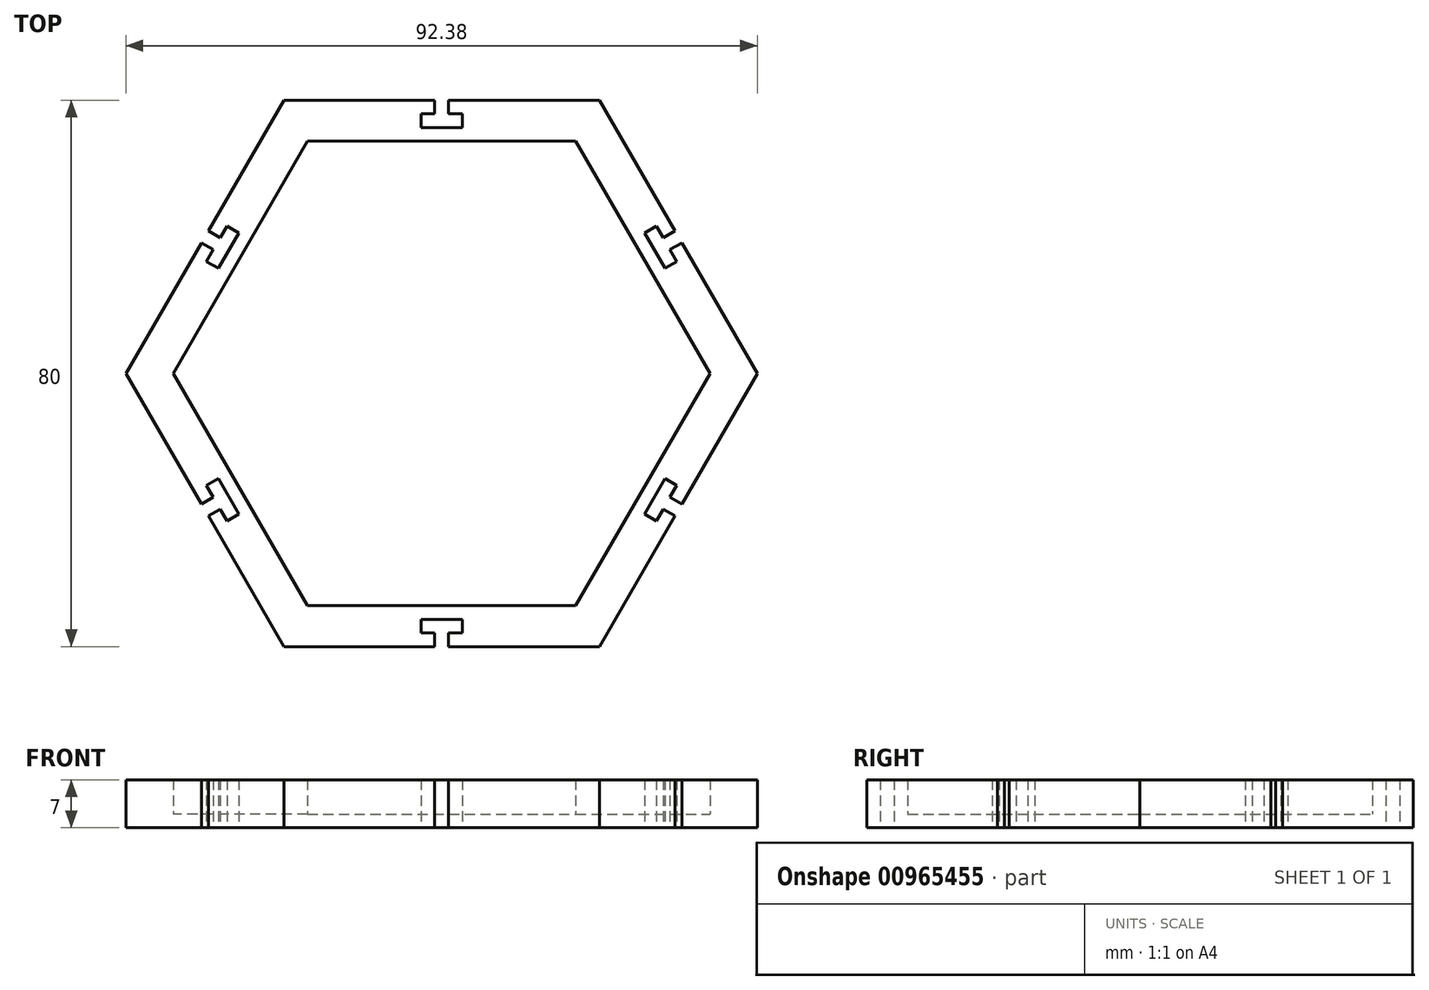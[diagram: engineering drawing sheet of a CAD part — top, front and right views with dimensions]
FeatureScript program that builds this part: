
annotation { "Feature Type Name" : "Feature", "Feature Type Description" : "" }
export const myFeature = defineFeature(function(context is Context, id is Id, definition is map)
    precondition{}
    {
        {
            var Q0;
            Q0=qCreatedBy(makeId("Top.planeOp"),FACE);
            var sketch = newSketch(context, id + "F0", { "sketchPlane" : qUnion([Q0])});
            skLineSegment(sketch, "E0", {"start": v(-13.7, -43.48) * mm, "end": v(8.4, -43.48) * mm});
            skLineSegment(sketch, "E1", {"start": v(9.4, -3.48) * mm, "end": v(9.4, -43.48) * mm, "construction": true});
            skLineSegment(sketch, "E2", {"start": v(8.4, -43.48) * mm, "end": v(8.4, -41.48) * mm});
            skLineSegment(sketch, "E3", {"start": v(8.4, -41.48) * mm, "end": v(6.4, -41.48) * mm});
            skLineSegment(sketch, "E4", {"start": v(6.4, -41.48) * mm, "end": v(6.4, -39.48) * mm});
            skLineSegment(sketch, "E5", {"start": v(6.4, -39.48) * mm, "end": v(12.4, -39.48) * mm});
            skLineSegment(sketch, "E6", {"start": v(12.4, -39.48) * mm, "end": v(12.4, -41.48) * mm});
            skLineSegment(sketch, "E7", {"start": v(12.4, -41.48) * mm, "end": v(10.4, -41.48) * mm});
            skLineSegment(sketch, "E8", {"start": v(10.4, -41.48) * mm, "end": v(10.4, -43.48) * mm});
            skLineSegment(sketch, "E9.trimOffspring", {"start": v(10.4, -43.48) * mm, "end": v(32.5, -43.48) * mm});
            skPoint(sketch, "E10", {"position": v(9.4, -39.48) * mm});
            skLineSegment(sketch, "E11.1.0", {"start": v(9.4, -3.48) * mm, "end": v(44.04, -23.48) * mm, "construction": true});
            skPoint(sketch, "E11.1.1", {"position": v(40.58, -21.48) * mm});
            skLineSegment(sketch, "E11.1.2", {"start": v(44.54, -22.62) * mm, "end": v(55.59, -3.48) * mm});
            skLineSegment(sketch, "E11.1.3", {"start": v(32.5, -43.48) * mm, "end": v(43.54, -24.35) * mm});
            skLineSegment(sketch, "E11.1.4", {"start": v(39.08, -24.08) * mm, "end": v(42.08, -18.88) * mm});
            skLineSegment(sketch, "E11.1.5", {"start": v(42.08, -18.88) * mm, "end": v(43.8, -19.88) * mm});
            skLineSegment(sketch, "E11.1.6", {"start": v(43.8, -19.88) * mm, "end": v(42.8, -21.62) * mm});
            skLineSegment(sketch, "E11.1.7", {"start": v(43.54, -24.35) * mm, "end": v(41.8, -23.35) * mm});
            skLineSegment(sketch, "E11.1.8", {"start": v(40.8, -25.08) * mm, "end": v(39.08, -24.08) * mm});
            skLineSegment(sketch, "E11.1.9", {"start": v(41.8, -23.35) * mm, "end": v(40.8, -25.08) * mm});
            skLineSegment(sketch, "E11.1.10", {"start": v(42.8, -21.62) * mm, "end": v(44.54, -22.62) * mm});
            skLineSegment(sketch, "E11.2.0", {"start": v(9.4, -3.48) * mm, "end": v(44.04, 16.52) * mm, "construction": true});
            skPoint(sketch, "E11.2.1", {"position": v(40.58, 14.52) * mm});
            skLineSegment(sketch, "E11.2.2", {"start": v(43.54, 17.38) * mm, "end": v(32.5, 36.52) * mm});
            skLineSegment(sketch, "E11.2.3", {"start": v(55.59, -3.48) * mm, "end": v(44.54, 15.65) * mm});
            skLineSegment(sketch, "E11.2.4", {"start": v(42.08, 11.92) * mm, "end": v(39.08, 17.12) * mm});
            skLineSegment(sketch, "E11.2.5", {"start": v(39.08, 17.12) * mm, "end": v(40.8, 18.12) * mm});
            skLineSegment(sketch, "E11.2.6", {"start": v(40.8, 18.12) * mm, "end": v(41.8, 16.38) * mm});
            skLineSegment(sketch, "E11.2.7", {"start": v(44.54, 15.65) * mm, "end": v(42.8, 14.65) * mm});
            skLineSegment(sketch, "E11.2.8", {"start": v(43.8, 12.92) * mm, "end": v(42.08, 11.92) * mm});
            skLineSegment(sketch, "E11.2.9", {"start": v(42.8, 14.65) * mm, "end": v(43.8, 12.92) * mm});
            skLineSegment(sketch, "E11.2.10", {"start": v(41.8, 16.38) * mm, "end": v(43.54, 17.38) * mm});
            skLineSegment(sketch, "E11.3.0", {"start": v(9.4, -3.48) * mm, "end": v(9.4, 36.52) * mm, "construction": true});
            skPoint(sketch, "E11.3.1", {"position": v(9.4, 32.52) * mm});
            skLineSegment(sketch, "E11.3.2", {"start": v(8.4, 36.52) * mm, "end": v(-13.7, 36.52) * mm});
            skLineSegment(sketch, "E11.3.3", {"start": v(32.5, 36.52) * mm, "end": v(10.4, 36.52) * mm});
            skLineSegment(sketch, "E11.3.4", {"start": v(12.4, 32.52) * mm, "end": v(6.4, 32.52) * mm});
            skLineSegment(sketch, "E11.3.5", {"start": v(6.4, 32.52) * mm, "end": v(6.4, 34.52) * mm});
            skLineSegment(sketch, "E11.3.6", {"start": v(6.4, 34.52) * mm, "end": v(8.4, 34.52) * mm});
            skLineSegment(sketch, "E11.3.7", {"start": v(10.4, 36.52) * mm, "end": v(10.4, 34.52) * mm});
            skLineSegment(sketch, "E11.3.8", {"start": v(12.4, 34.52) * mm, "end": v(12.4, 32.52) * mm});
            skLineSegment(sketch, "E11.3.9", {"start": v(10.4, 34.52) * mm, "end": v(12.4, 34.52) * mm});
            skLineSegment(sketch, "E11.3.10", {"start": v(8.4, 34.52) * mm, "end": v(8.4, 36.52) * mm});
            skLineSegment(sketch, "E11.4.0", {"start": v(9.4, -3.48) * mm, "end": v(-25.24, 16.52) * mm, "construction": true});
            skPoint(sketch, "E11.4.1", {"position": v(-21.78, 14.52) * mm});
            skLineSegment(sketch, "E11.4.2", {"start": v(-25.74, 15.65) * mm, "end": v(-36.79, -3.48) * mm});
            skLineSegment(sketch, "E11.4.3", {"start": v(-13.7, 36.52) * mm, "end": v(-24.74, 17.38) * mm});
            skLineSegment(sketch, "E11.4.4", {"start": v(-20.28, 17.12) * mm, "end": v(-23.28, 11.92) * mm});
            skLineSegment(sketch, "E11.4.5", {"start": v(-23.28, 11.92) * mm, "end": v(-25, 12.92) * mm});
            skLineSegment(sketch, "E11.4.6", {"start": v(-25, 12.92) * mm, "end": v(-24, 14.65) * mm});
            skLineSegment(sketch, "E11.4.7", {"start": v(-24.74, 17.38) * mm, "end": v(-23, 16.38) * mm});
            skLineSegment(sketch, "E11.4.8", {"start": v(-22, 18.12) * mm, "end": v(-20.28, 17.12) * mm});
            skLineSegment(sketch, "E11.4.9", {"start": v(-23, 16.38) * mm, "end": v(-22, 18.12) * mm});
            skLineSegment(sketch, "E11.4.10", {"start": v(-24, 14.65) * mm, "end": v(-25.74, 15.65) * mm});
            skLineSegment(sketch, "E11.5.0", {"start": v(9.4, -3.48) * mm, "end": v(-25.24, -23.48) * mm, "construction": true});
            skPoint(sketch, "E11.5.1", {"position": v(-21.78, -21.48) * mm});
            skLineSegment(sketch, "E11.5.2", {"start": v(-24.74, -24.35) * mm, "end": v(-13.7, -43.48) * mm});
            skLineSegment(sketch, "E11.5.3", {"start": v(-36.79, -3.48) * mm, "end": v(-25.74, -22.62) * mm});
            skLineSegment(sketch, "E11.5.4", {"start": v(-23.28, -18.88) * mm, "end": v(-20.28, -24.08) * mm});
            skLineSegment(sketch, "E11.5.5", {"start": v(-20.28, -24.08) * mm, "end": v(-22, -25.08) * mm});
            skLineSegment(sketch, "E11.5.6", {"start": v(-22, -25.08) * mm, "end": v(-23, -23.35) * mm});
            skLineSegment(sketch, "E11.5.7", {"start": v(-25.74, -22.62) * mm, "end": v(-24, -21.62) * mm});
            skLineSegment(sketch, "E11.5.8", {"start": v(-25, -19.88) * mm, "end": v(-23.28, -18.88) * mm});
            skLineSegment(sketch, "E11.5.9", {"start": v(-24, -21.62) * mm, "end": v(-25, -19.88) * mm});
            skLineSegment(sketch, "E11.5.10", {"start": v(-23, -23.35) * mm, "end": v(-24.74, -24.35) * mm});
            skPoint(sketch, "E11.center", {"position": v(9.4, -3.48) * mm});
            skSolve(sketch);
        }
        {
            var Q0;
            Q0=makeQuery(id+"F0.imprint","IMPRINT",FACE,{"disambiguationData":[TD([[makeQuery(id+"F0.imprint","IMPRINT",EDGE,{"derivedFrom":sQuery(id+"F0.wireOp",EDGE,"E0")}),1.0]])]});
            extrude(context, id + "F1", {"entities" : qUnion([Q0]), "depth" : 2 * mm, "offsetDistance" : 25 * mm});
        }
        {
            var Q0;
            Q0=makeQuery(id+"F1.opExtrude","CAP_FACE",FACE,{"disambiguationData":[OSD([sQuery(id+"F0.wireOp",EDGE,"E0"),sQuery(id+"F0.wireOp",EDGE,"E2"),sQuery(id+"F0.wireOp",EDGE,"E3"),sQuery(id+"F0.wireOp",EDGE,"E4"),sQuery(id+"F0.wireOp",EDGE,"E5"),sQuery(id+"F0.wireOp",EDGE,"E6"),sQuery(id+"F0.wireOp",EDGE,"E7"),sQuery(id+"F0.wireOp",EDGE,"E8"),sQuery(id+"F0.wireOp",EDGE,"E9.trimOffspring"),sQuery(id+"F0.wireOp",EDGE,"E11.1.2"),sQuery(id+"F0.wireOp",EDGE,"E11.1.3"),sQuery(id+"F0.wireOp",EDGE,"E11.1.4"),sQuery(id+"F0.wireOp",EDGE,"E11.1.5"),sQuery(id+"F0.wireOp",EDGE,"E11.1.6"),sQuery(id+"F0.wireOp",EDGE,"E11.1.7"),sQuery(id+"F0.wireOp",EDGE,"E11.1.8"),sQuery(id+"F0.wireOp",EDGE,"E11.1.9"),sQuery(id+"F0.wireOp",EDGE,"E11.1.10"),sQuery(id+"F0.wireOp",EDGE,"E11.2.2"),sQuery(id+"F0.wireOp",EDGE,"E11.2.3"),sQuery(id+"F0.wireOp",EDGE,"E11.2.4"),sQuery(id+"F0.wireOp",EDGE,"E11.2.5"),sQuery(id+"F0.wireOp",EDGE,"E11.2.6"),sQuery(id+"F0.wireOp",EDGE,"E11.2.7"),sQuery(id+"F0.wireOp",EDGE,"E11.2.8"),sQuery(id+"F0.wireOp",EDGE,"E11.2.9"),sQuery(id+"F0.wireOp",EDGE,"E11.2.10"),sQuery(id+"F0.wireOp",EDGE,"E11.3.2"),sQuery(id+"F0.wireOp",EDGE,"E11.3.3"),sQuery(id+"F0.wireOp",EDGE,"E11.3.4"),sQuery(id+"F0.wireOp",EDGE,"E11.3.5"),sQuery(id+"F0.wireOp",EDGE,"E11.3.6"),sQuery(id+"F0.wireOp",EDGE,"E11.3.7"),sQuery(id+"F0.wireOp",EDGE,"E11.3.8"),sQuery(id+"F0.wireOp",EDGE,"E11.3.9"),sQuery(id+"F0.wireOp",EDGE,"E11.3.10"),sQuery(id+"F0.wireOp",EDGE,"E11.4.2"),sQuery(id+"F0.wireOp",EDGE,"E11.4.3"),sQuery(id+"F0.wireOp",EDGE,"E11.4.4"),sQuery(id+"F0.wireOp",EDGE,"E11.4.5"),sQuery(id+"F0.wireOp",EDGE,"E11.4.6"),sQuery(id+"F0.wireOp",EDGE,"E11.4.7"),sQuery(id+"F0.wireOp",EDGE,"E11.4.8"),sQuery(id+"F0.wireOp",EDGE,"E11.4.9"),sQuery(id+"F0.wireOp",EDGE,"E11.4.10"),sQuery(id+"F0.wireOp",EDGE,"E11.5.2"),sQuery(id+"F0.wireOp",EDGE,"E11.5.3"),sQuery(id+"F0.wireOp",EDGE,"E11.5.4"),sQuery(id+"F0.wireOp",EDGE,"E11.5.5"),sQuery(id+"F0.wireOp",EDGE,"E11.5.6"),sQuery(id+"F0.wireOp",EDGE,"E11.5.7"),sQuery(id+"F0.wireOp",EDGE,"E11.5.8"),sQuery(id+"F0.wireOp",EDGE,"E11.5.9"),sQuery(id+"F0.wireOp",EDGE,"E11.5.10")])],"isStart":false});
            var sketch = newSketch(context, id + "F2", { "sketchPlane" : qUnion([Q0])});
            skPoint(sketch, "E12.0", {"position": v(9.4, -3.48) * mm});
            skCircle(sketch, "E13.cCircle", {"center": v(9.4, -3.48) * mm, "radius": 34 * mm, "construction": true});
            skLineSegment(sketch, "E13.0", {"start": v(-29.86, -3.48) * mm, "end": v(-10.23, 30.52) * mm});
            skLineSegment(sketch, "E13.1", {"start": v(-10.23, 30.52) * mm, "end": v(29.03, 30.52) * mm});
            skLineSegment(sketch, "E13.2", {"start": v(29.03, 30.52) * mm, "end": v(48.66, -3.48) * mm});
            skLineSegment(sketch, "E13.3", {"start": v(48.66, -3.48) * mm, "end": v(29.03, -37.48) * mm});
            skLineSegment(sketch, "E13.4", {"start": v(29.03, -37.48) * mm, "end": v(-10.23, -37.48) * mm});
            skLineSegment(sketch, "E13.5", {"start": v(-10.23, -37.48) * mm, "end": v(-29.86, -3.48) * mm});
            skPoint(sketch, "E13.0.midPoint", {"position": v(-20.04, 13.52) * mm});
            skSolve(sketch);
        }
        {
            var Q0;
            Q0=makeQuery(id+"F2.imprint","IMPRINT",FACE,{"disambiguationData":[TD([[makeQuery(id+"F2.imprint","IMPRINT",EDGE,{"derivedFrom":sQuery(id+"F2.wireOp",EDGE,"E13.0")}),1.0]])]});
            extrude(context, id + "F3", {"entities" : qUnion([Q0]), "operationType" : NewBodyOperationType.ADD, "depth" : 5 * mm, "offsetDistance" : 25 * mm});
        }
    });
